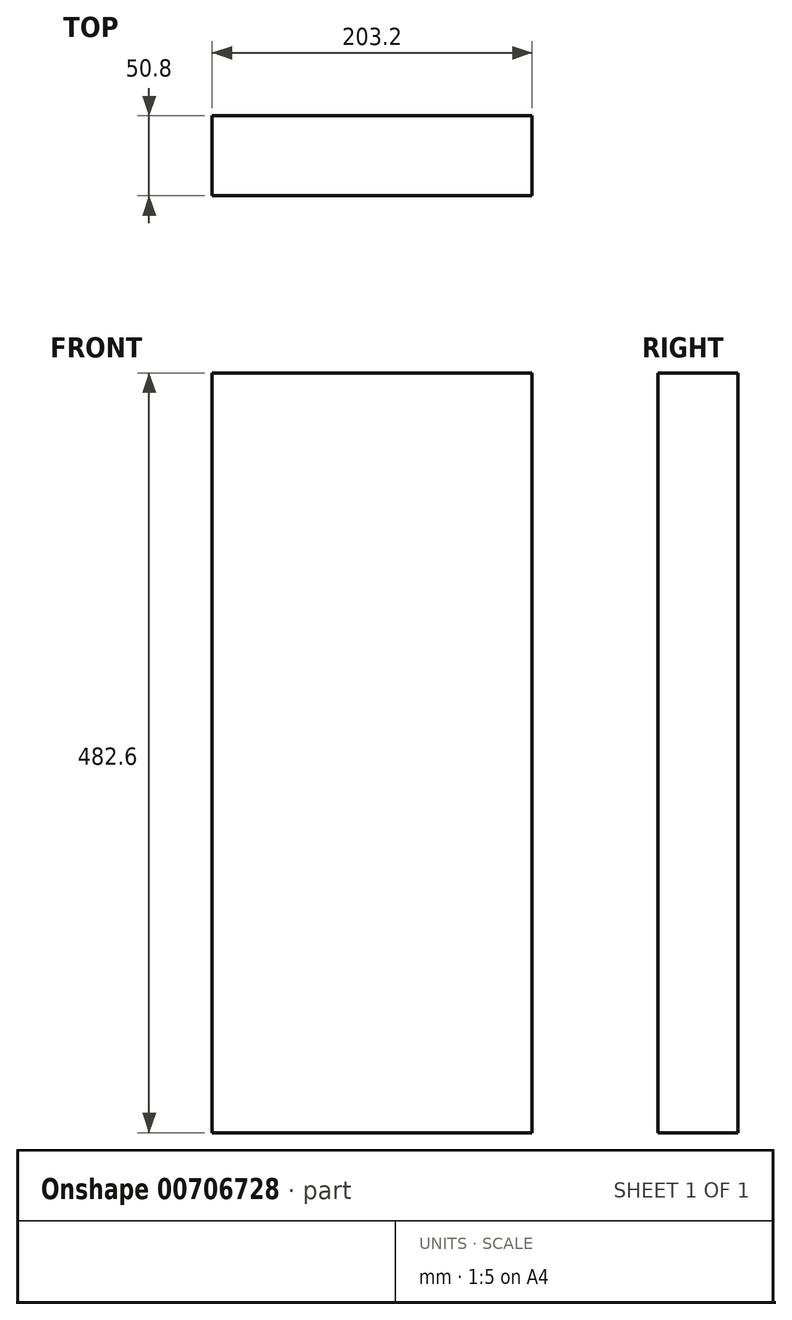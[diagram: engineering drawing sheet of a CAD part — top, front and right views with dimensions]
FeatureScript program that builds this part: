
annotation { "Feature Type Name" : "Feature", "Feature Type Description" : "" }
export const myFeature = defineFeature(function(context is Context, id is Id, definition is map)
    precondition{}
    {
        {
            var Q0;
            Q0=qCreatedBy(makeId("Top.planeOp"),FACE);
            var sketch = newSketch(context, id + "F0", { "sketchPlane" : qUnion([Q0])});
            skLineSegment(sketch, "E0.bottom", {"start": v(101.6, -25.4) * mm, "end": v(-101.6, -25.4) * mm});
            skLineSegment(sketch, "E0.top", {"start": v(101.6, 25.4) * mm, "end": v(-101.6, 25.4) * mm});
            skLineSegment(sketch, "E0.left", {"start": v(101.6, -25.4) * mm, "end": v(101.6, 25.4) * mm});
            skLineSegment(sketch, "E0.right", {"start": v(-101.6, -25.4) * mm, "end": v(-101.6, 25.4) * mm});
            skPoint(sketch, "E0.middle", {"position": v(0, 0) * mm});
            skSolve(sketch);
        }
        {
            var Q0;
            Q0=makeQuery(id+"F0.imprint","IMPRINT",FACE,{"disambiguationData":[TD([[makeQuery(id+"F0.imprint","IMPRINT",EDGE,{"derivedFrom":sQuery(id+"F0.wireOp",EDGE,"E0.bottom")}),-1.0]])]});
            extrude(context, id + "F1", {"entities" : qUnion([Q0]), "depth" : 482.6 * mm, "offsetDistance" : 25.4 * mm});
        }
    });
